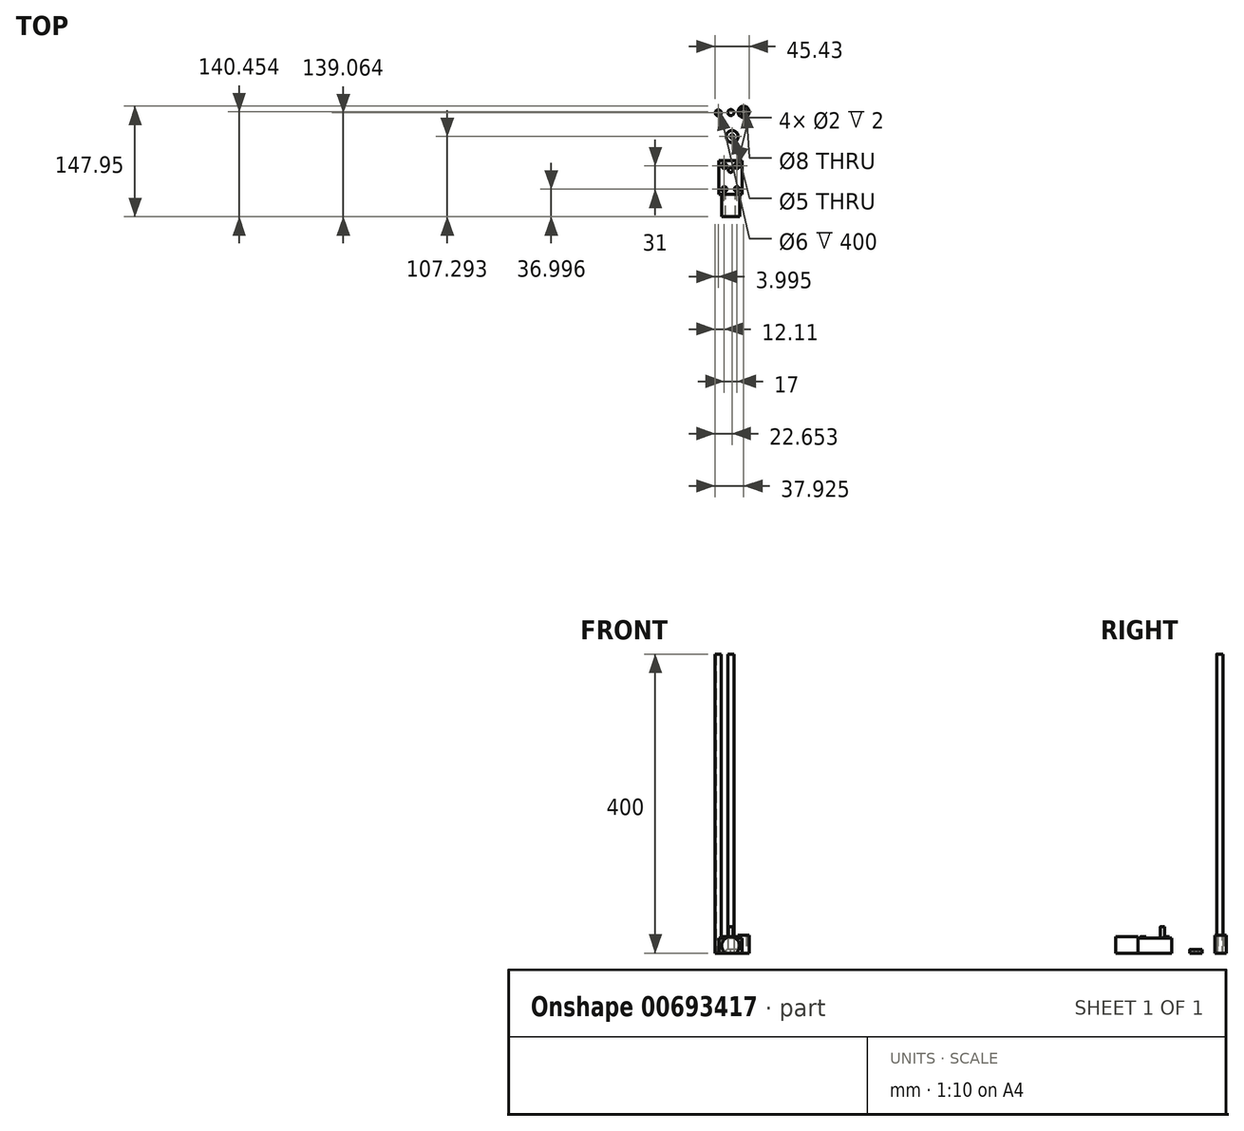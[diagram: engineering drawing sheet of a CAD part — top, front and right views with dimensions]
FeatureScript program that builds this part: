
annotation { "Feature Type Name" : "Feature", "Feature Type Description" : "" }
export const myFeature = defineFeature(function(context is Context, id is Id, definition is map)
    precondition{}
    {
        {
            var Q0;
            Q0=qCreatedBy(makeId("Top.planeOp"),FACE);
            var sketch = newSketch(context, id + "F0", { "sketchPlane" : qUnion([Q0])});
            skCircle(sketch, "E0", {"center": v(-63.17, 63.04) * mm, "radius": 4 * mm});
            skCircle(sketch, "E1", {"center": v(-46.24, 63.45) * mm, "radius": 4 * mm});
            skCircle(sketch, "E2.0", {"center": v(-63.17, 63.04) * mm, "radius": 3 * mm});
            skCircle(sketch, "E3", {"center": v(-29.24, 64.43) * mm, "radius": 4 * mm});
            skCircle(sketch, "E4.0", {"center": v(-29.24, 64.43) * mm, "radius": 7.5 * mm});
            skCircle(sketch, "E5", {"center": v(-44.52, 31.27) * mm, "radius": 2.5 * mm});
            skCircle(sketch, "E6.0", {"center": v(-44.52, 31.27) * mm, "radius": 8 * mm});
            skSolve(sketch);
        }
        {
            var Q0;
            Q0=makeQuery(id+"F0.imprint","IMPRINT",FACE,{"disambiguationData":[TD([[makeQuery(id+"F0.imprint","IMPRINT",EDGE,{"derivedFrom":sQuery(id+"F0.wireOp",EDGE,"E0")}),1.0]])]});
            var Q1;
            Q1=makeQuery(id+"F0.imprint","IMPRINT",FACE,{"disambiguationData":[TD([[makeQuery(id+"F0.imprint","IMPRINT",EDGE,{"derivedFrom":sQuery(id+"F0.wireOp",EDGE,"E1")}),1.0]])]});
            extrude(context, id + "F1", {"entities" : qUnion([Q0, Q1]), "depth" : 400 * mm, "offsetDistance" : 25 * mm});
        }
        {
            var Q0;
            Q0=makeQuery(id+"F0.imprint","IMPRINT",FACE,{"disambiguationData":[TD([[makeQuery(id+"F0.imprint","IMPRINT",EDGE,{"derivedFrom":sQuery(id+"F0.wireOp",EDGE,"E3")}),-1.0]])]});
            extrude(context, id + "F2", {"entities" : qUnion([Q0]), "depth" : 24 * mm, "offsetDistance" : 25 * mm});
        }
        {
            var Q0;
            Q0=qCreatedBy(makeId("Top.planeOp"),FACE);
            var sketch = newSketch(context, id + "F3", { "sketchPlane" : qUnion([Q0])});
            skLineSegment(sketch, "E7.bottom", {"start": v(-62.06, -1.02) * mm, "end": v(-31.06, -1.02) * mm});
            skLineSegment(sketch, "E7.top", {"start": v(-62.06, -46.02) * mm, "end": v(-31.06, -46.02) * mm});
            skLineSegment(sketch, "E7.left", {"start": v(-62.06, -1.02) * mm, "end": v(-62.06, -46.02) * mm});
            skLineSegment(sketch, "E7.right", {"start": v(-31.06, -1.02) * mm, "end": v(-31.06, -46.02) * mm});
            skSolve(sketch);
        }
        {
            var Q0;
            Q0=makeQuery(id+"F3.imprint","IMPRINT",FACE,{"disambiguationData":[TD([[makeQuery(id+"F3.imprint","IMPRINT",EDGE,{"derivedFrom":sQuery(id+"F3.wireOp",EDGE,"E7.bottom")}),-1.0]])]});
            extrude(context, id + "F4", {"entities" : qUnion([Q0]), "depth" : 20 * mm, "offsetDistance" : 25 * mm});
        }
        {
            var Q0;
            Q0=makeQuery(id+"F4.opExtrude","SWEPT_FACE",FACE,{"disambiguationData":[OSD([sQuery(id+"F3.wireOp",EDGE,"E7.top")])]});
            var sketch = newSketch(context, id + "F5", { "sketchPlane" : qUnion([Q0])});
            skCircle(sketch, "E8", {"center": v(-46.56, 10) * mm, "radius": 12 * mm});
            skPoint(sketch, "E8.centerSnap0", {"position": v(-62.06, 10) * mm});
            skPoint(sketch, "E8.centerSnap1", {"position": v(-46.56, 20) * mm});
            skSolve(sketch);
        }
        {
            var Q0;
            {var subQ0=sQuery(id+"F5.wireOp",EDGE,"E8");var subQ1=sQuery(id+"F3.wireOp",EDGE,"E7.top");var subQ2=makeQuery(id+"F4.opExtrude","CAP_EDGE",EDGE,{"disambiguationData":[OSD([subQ1])],"isStart":false});var subQ3=makeQuery(id+"F5.imprint","INTERSECT",VERTEX,{"disambiguationData":[OD(0.0)],"derivedFrom":[subQ2,subQ0]});Q0=makeQuery(id+"F5.imprint","IMPRINT",FACE,{"disambiguationData":[TD([[makeQuery(id+"F5.imprint","IMPRINT",EDGE,{"disambiguationData":[TD([[subQ3,-1.0]])],"derivedFrom":subQ0}),1.0]])]});}
            var Q1;
            {var subQ0=sQuery(id+"F5.wireOp",EDGE,"E8");var subQ1=makeQuery(id+"F4.opExtrude","CAP_EDGE",EDGE,{"disambiguationData":[OSD([sQuery(id+"F3.wireOp",EDGE,"E7.top")])],"isStart":false});var subQ2=makeQuery(id+"F5.imprint","INTERSECT",VERTEX,{"disambiguationData":[OD(0.0)],"derivedFrom":[subQ1,subQ0]});Q1=makeQuery(id+"F5.imprint","IMPRINT",FACE,{"disambiguationData":[TD([[makeQuery(id+"F5.imprint","IMPRINT",EDGE,{"disambiguationData":[TD([[subQ2,1.0]])],"derivedFrom":subQ0}),1.0]])]});}
            var Q2;
            {var subQ0=sQuery(id+"F5.wireOp",EDGE,"E8");var subQ1=makeQuery(id+"F4.opExtrude","CAP_EDGE",EDGE,{"disambiguationData":[OSD([sQuery(id+"F3.wireOp",EDGE,"E7.top")])],"isStart":true});var subQ2=makeQuery(id+"F5.imprint","INTERSECT",VERTEX,{"disambiguationData":[OD(0.0)],"derivedFrom":[subQ1,subQ0]});Q2=makeQuery(id+"F5.imprint","IMPRINT",FACE,{"disambiguationData":[TD([[makeQuery(id+"F5.imprint","IMPRINT",EDGE,{"disambiguationData":[TD([[subQ2,-1.0]])],"derivedFrom":subQ0}),1.0]])]});}
            extrude(context, id + "F6", {"entities" : qUnion([Q0, Q1, Q2]), "operationType" : NewBodyOperationType.ADD, "depth" : 30 * mm, "offsetDistance" : 25 * mm});
        }
        {
            var Q0;
            Q0=makeQuery(id+"F4.opExtrude","CAP_FACE",FACE,{"disambiguationData":[OSD([sQuery(id+"F3.wireOp",EDGE,"E7.bottom"),sQuery(id+"F3.wireOp",EDGE,"E7.top"),sQuery(id+"F3.wireOp",EDGE,"E7.left"),sQuery(id+"F3.wireOp",EDGE,"E7.right")])],"isStart":false});
            var sketch = newSketch(context, id + "F7", { "sketchPlane" : qUnion([Q0])});
            skSolve(sketch);
        }
        {
            var Q0;
            {var subQ6=sQuery(id+"F3.wireOp",EDGE,"E7.bottom");Q0=makeQuery(id+"F7.imprint","IMPRINT",FACE,{"disambiguationData":[TD([[makeQuery(id+"F7.imprint","IMPRINT",EDGE,{"derivedFrom":makeQuery(id+"F4.opExtrude","CAP_EDGE",EDGE,{"disambiguationData":[OSD([subQ6])],"isStart":false})}),-1.0]])]});}
            var sketch = newSketch(context, id + "F8", { "sketchPlane" : qUnion([Q0])});
            skCircle(sketch, "E9", {"center": v(-55.06, -8.02) * mm, "radius": 3.5 * mm});
            skCircle(sketch, "E10.0", {"center": v(-55.06, -8.02) * mm, "radius": 1 * mm});
            skCircle(sketch, "E11.0.1.0", {"center": v(-55.06, -39.02) * mm, "radius": 3.5 * mm});
            skCircle(sketch, "E11.0.1.1", {"center": v(-55.06, -39.02) * mm, "radius": 1 * mm});
            skCircle(sketch, "E11.1.0.0", {"center": v(-38.06, -8.02) * mm, "radius": 3.5 * mm});
            skCircle(sketch, "E11.1.0.1", {"center": v(-38.06, -8.02) * mm, "radius": 1 * mm});
            skCircle(sketch, "E11.1.1.0", {"center": v(-38.06, -39.02) * mm, "radius": 3.5 * mm});
            skCircle(sketch, "E11.1.1.1", {"center": v(-38.06, -39.02) * mm, "radius": 1 * mm});
            skLineSegment(sketch, "E11.direction1", {"start": v(-55.06, -8.02) * mm, "end": v(-38.06, -8.02) * mm, "construction": true});
            skLineSegment(sketch, "E11.direction2", {"start": v(-55.06, -8.02) * mm, "end": v(-55.06, -39.02) * mm, "construction": true});
            skCircle(sketch, "E12", {"center": v(-46.56, -13.48) * mm, "radius": 3 * mm});
            skSolve(sketch);
        }
        {
            var Q0;
            Q0=makeQuery(id+"F8.imprint","IMPRINT",FACE,{"disambiguationData":[TD([[makeQuery(id+"F8.imprint","IMPRINT",EDGE,{"derivedFrom":sQuery(id+"F8.wireOp",EDGE,"E9")}),1.0]])]});
            var Q1;
            Q1=makeQuery(id+"F8.imprint","IMPRINT",FACE,{"disambiguationData":[TD([[makeQuery(id+"F8.imprint","IMPRINT",EDGE,{"derivedFrom":sQuery(id+"F8.wireOp",EDGE,"E11.1.0.0")}),1.0]])]});
            var Q2;
            Q2=makeQuery(id+"F8.imprint","IMPRINT",FACE,{"disambiguationData":[TD([[makeQuery(id+"F8.imprint","IMPRINT",EDGE,{"derivedFrom":sQuery(id+"F8.wireOp",EDGE,"E11.1.1.0")}),1.0]])]});
            var Q3;
            Q3=makeQuery(id+"F8.imprint","IMPRINT",FACE,{"disambiguationData":[TD([[makeQuery(id+"F8.imprint","IMPRINT",EDGE,{"derivedFrom":sQuery(id+"F8.wireOp",EDGE,"E11.0.1.0")}),1.0]])]});
            extrude(context, id + "F9", {"entities" : qUnion([Q0, Q1, Q2, Q3]), "operationType" : NewBodyOperationType.ADD, "depth" : 2 * mm, "offsetDistance" : 25 * mm});
        }
        {
            var Q0;
            Q0=makeQuery(id+"F8.imprint","IMPRINT",FACE,{"disambiguationData":[TD([[makeQuery(id+"F8.imprint","IMPRINT",EDGE,{"derivedFrom":sQuery(id+"F8.wireOp",EDGE,"E12")}),1.0]])]});
            extrude(context, id + "F10", {"entities" : qUnion([Q0]), "operationType" : NewBodyOperationType.ADD, "depth" : 15 * mm, "offsetDistance" : 25 * mm});
        }
        {
            var Q0;
            Q0=makeQuery(id+"F0.imprint","IMPRINT",FACE,{"disambiguationData":[TD([[makeQuery(id+"F0.imprint","IMPRINT",EDGE,{"derivedFrom":sQuery(id+"F0.wireOp",EDGE,"E5")}),-1.0]])]});
            extrude(context, id + "F11", {"entities" : qUnion([Q0]), "depth" : 5 * mm, "offsetDistance" : 25 * mm});
        }
    });
